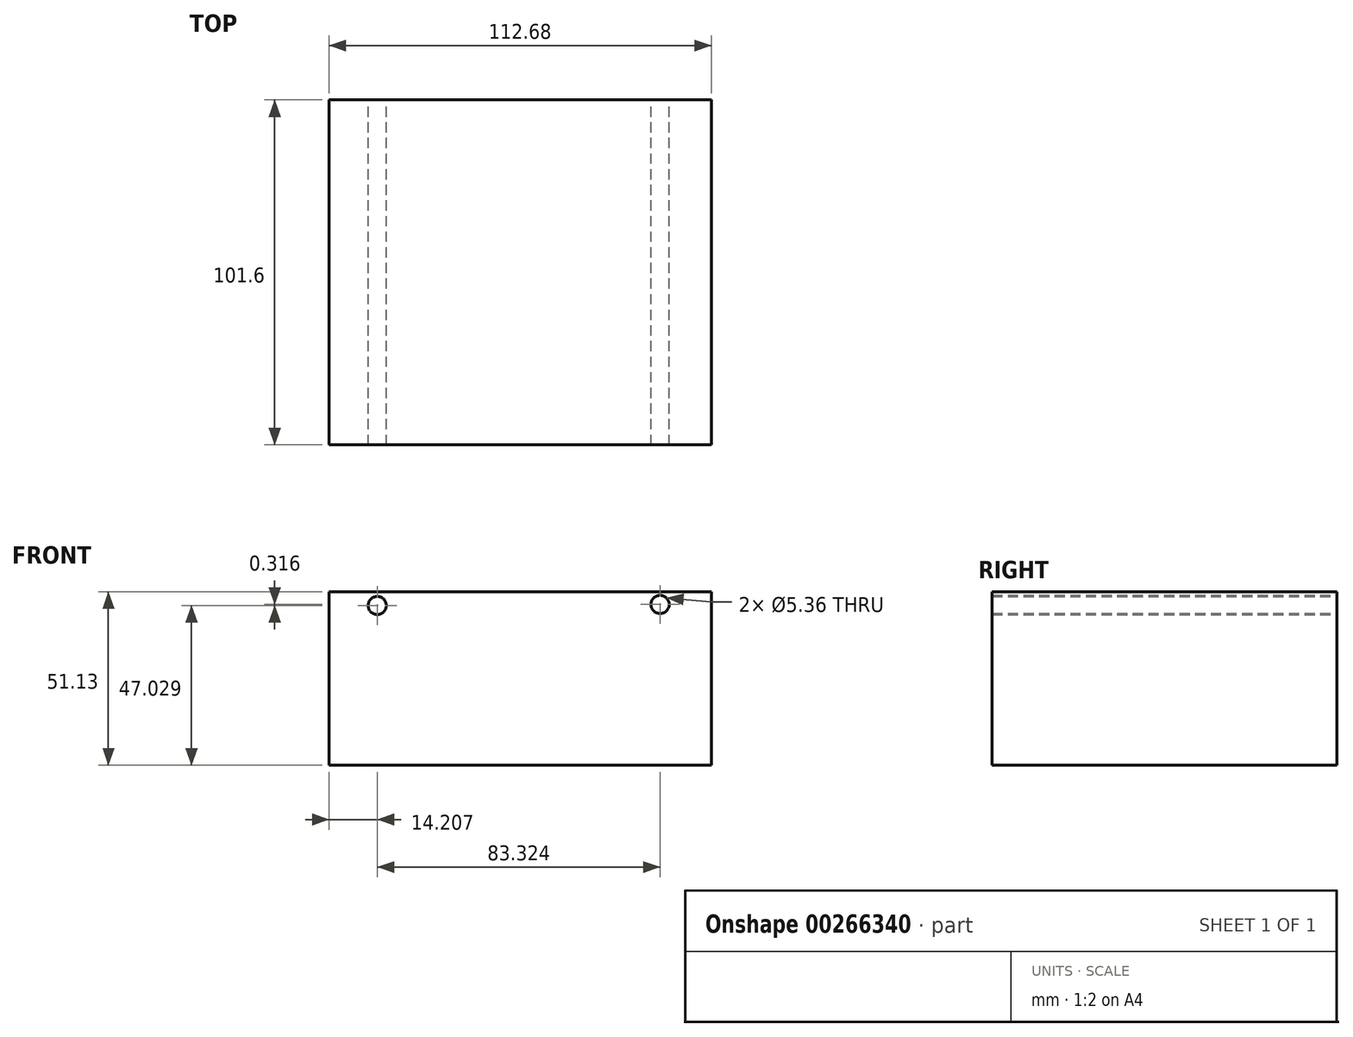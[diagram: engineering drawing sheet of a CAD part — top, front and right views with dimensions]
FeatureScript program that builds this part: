
annotation { "Feature Type Name" : "Feature", "Feature Type Description" : "" }
export const myFeature = defineFeature(function(context is Context, id is Id, definition is map)
    precondition{}
    {
        {
            var Q0;
            Q0=qCreatedBy(makeId("Front.planeOp"),FACE);
            var sketch = newSketch(context, id + "F0", { "sketchPlane" : qUnion([Q0])});
            skLineSegment(sketch, "E0", {"start": v(-56.5, 20.04) * mm, "end": v(56.18, 20.04) * mm});
            skLineSegment(sketch, "E1", {"start": v(56.18, 20.04) * mm, "end": v(56.18, -31.09) * mm});
            skLineSegment(sketch, "E2", {"start": v(56.18, -31.09) * mm, "end": v(-56.5, -31.09) * mm});
            skLineSegment(sketch, "E3", {"start": v(-56.5, -31.09) * mm, "end": v(-56.5, 20.04) * mm});
            skCircle(sketch, "E4", {"center": v(-42.3, 15.94) * mm, "radius": 2.68 * mm});
            skCircle(sketch, "E5", {"center": v(41.03, 16.25) * mm, "radius": 2.68 * mm});
            skLineSegment(sketch, "E6", {"start": v(-42.37, 18.62) * mm, "end": v(-42.37, 20.04) * mm});
            skSolve(sketch);
        }
        {
            var Q0;
            Q0 = qSketchRegion(id + "F0", true);
            var Q1;
            Q1=makeQuery(id+"F0.imprint","IMPRINT",FACE,{"disambiguationData":[TD([[makeQuery(id+"F0.imprint","IMPRINT",EDGE,{"derivedFrom":sQuery(id+"F0.wireOp",EDGE,"E0")}),-1.0]])]});
            extrude(context, id + "F1", {"entities" : qUnion([Q0, Q1]), "depth" : 3.17 * mm});
        }
        {
            var Q0;
            Q0 = qSketchRegion(id + "F0", true);
            extrude(context, id + "F2", {"entities" : qUnion([Q0]), "operationType" : NewBodyOperationType.ADD, "depth" : 101.6 * mm});
        }
    });
